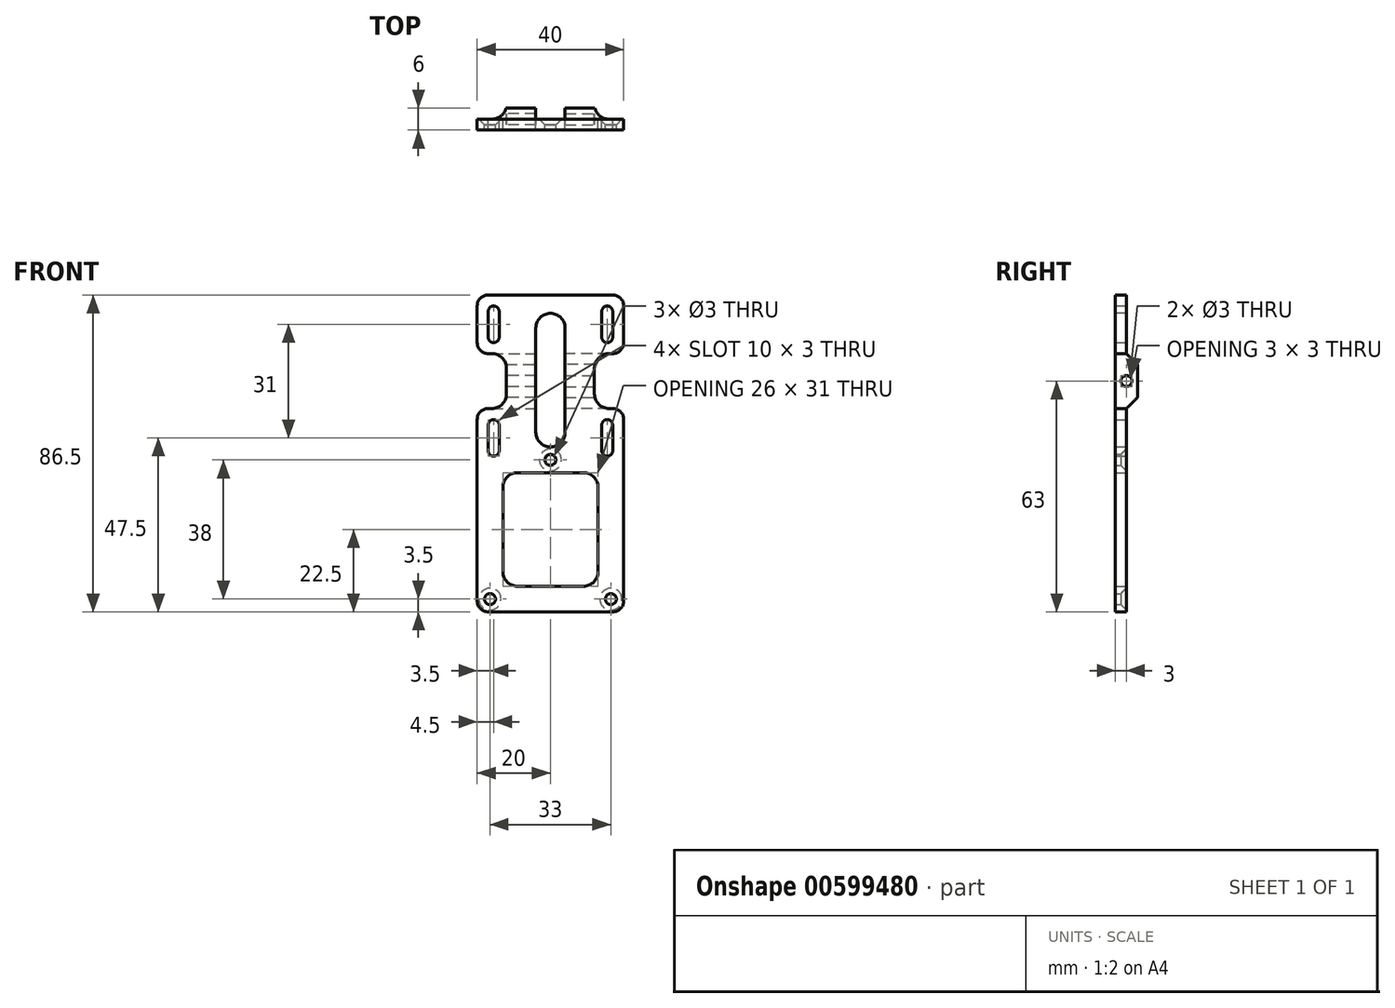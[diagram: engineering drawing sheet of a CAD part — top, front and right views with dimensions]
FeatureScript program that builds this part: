
annotation { "Feature Type Name" : "Feature", "Feature Type Description" : "" }
export const myFeature = defineFeature(function(context is Context, id is Id, definition is map)
    precondition{}
    {
        {
            var Q0;
            Q0=qCreatedBy(makeId("Front.planeOp"),FACE);
            var sketch = newSketch(context, id + "F0", { "sketchPlane" : qUnion([Q0])});
            skLineSegment(sketch, "E0.bottom", {"start": v(0, 43.25) * mm, "end": v(-20, 43.25) * mm});
            skLineSegment(sketch, "E0.top", {"start": v(0, -43.25) * mm, "end": v(-20, -43.25) * mm});
            skLineSegment(sketch, "E0.left", {"start": v(0, 43.25) * mm, "end": v(0, -43.25) * mm});
            skLineSegment(sketch, "E0.right", {"start": v(-20, 43.25) * mm, "end": v(-20, -43.25) * mm});
            skPoint(sketch, "E1", {"position": v(0, 0) * mm});
            skPoint(sketch, "E2", {"position": v(-16.5, -39.75) * mm});
            skPoint(sketch, "E3", {"position": v(0, -1.75) * mm});
            skLineSegment(sketch, "E4.bottom", {"start": v(-14, -0.75) * mm, "end": v(-17, -0.75) * mm});
            skLineSegment(sketch, "E4.top", {"start": v(-14, 9.25) * mm, "end": v(-17, 9.25) * mm});
            skLineSegment(sketch, "E4.left", {"start": v(-14, -0.75) * mm, "end": v(-14, 9.25) * mm});
            skLineSegment(sketch, "E4.right", {"start": v(-17, -0.75) * mm, "end": v(-17, 9.25) * mm});
            skLineSegment(sketch, "E5", {"start": v(0, 19.75) * mm, "end": v(-20, 19.75) * mm, "construction": true});
            skPoint(sketch, "E6", {"position": v(-14, 4.25) * mm});
            skLineSegment(sketch, "E7.MirrorCS", {"start": v(-14, 30.25) * mm, "end": v(-17, 30.25) * mm});
            skLineSegment(sketch, "E8.MirrorCS", {"start": v(-14, 40.25) * mm, "end": v(-14, 30.25) * mm});
            skLineSegment(sketch, "E9.MirrorCS", {"start": v(-17, 40.25) * mm, "end": v(-17, 30.25) * mm});
            skLineSegment(sketch, "E10.MirrorCS", {"start": v(-14, 40.25) * mm, "end": v(-17, 40.25) * mm});
            skLineSegment(sketch, "E11", {"start": v(0, 38.25) * mm, "end": v(-4, 38.25) * mm});
            skLineSegment(sketch, "E12", {"start": v(-4, 38.25) * mm, "end": v(-4, 1.75) * mm});
            skLineSegment(sketch, "E13", {"start": v(-4, 1.75) * mm, "end": v(0, 1.75) * mm});
            skLineSegment(sketch, "E14", {"start": v(0, -36.25) * mm, "end": v(-13, -36.25) * mm});
            skLineSegment(sketch, "E15", {"start": v(-13, -36.25) * mm, "end": v(-13, -5.25) * mm});
            skLineSegment(sketch, "E16", {"start": v(-13, -5.25) * mm, "end": v(0, -5.25) * mm});
            skPoint(sketch, "E17", {"position": v(-15.5, -0.75) * mm});
            skLineSegment(sketch, "E18", {"start": v(-20, 12.25) * mm, "end": v(-12, 12.25) * mm});
            skLineSegment(sketch, "E19", {"start": v(-12, 12.25) * mm, "end": v(-12, 19.75) * mm});
            skLineSegment(sketch, "E20.MirrorCS", {"start": v(-12, 27.25) * mm, "end": v(-12, 19.75) * mm});
            skLineSegment(sketch, "E21.MirrorCS", {"start": v(-20, 27.25) * mm, "end": v(-12, 27.25) * mm});
            skLineSegment(sketch, "E22", {"start": v(-12, 27.25) * mm, "end": v(-4, 27.25) * mm});
            skLineSegment(sketch, "E23", {"start": v(-12, 12.25) * mm, "end": v(-4, 12.25) * mm});
            skSolve(sketch);
        }
        {
            var Q0;
            Q0=makeQuery(id+"F0.imprint","IMPRINT",FACE,{"disambiguationData":[TD([[makeQuery(id+"F0.imprint","IMPRINT",EDGE,{"derivedFrom":sQuery(id+"F0.wireOp",EDGE,"E0.bottom")}),1.0]])]});
            var Q1;
            {var subQ0=sQuery(id+"F0.wireOp",EDGE,"vfTZMCeK-eEZJ-BKLE-hduP-PeNeDjFpHONc");Q1=makeQuery(id+"F0.imprint","IMPRINT",FACE,{"disambiguationData":[TD([[makeQuery(id+"F0.imprint","IMPRINT",EDGE,{"derivedFrom":subQ0}),-1.0]])]});}
            var Q2;
            {var subQ3=sQuery(id+"F0.wireOp",EDGE,"E0.top");Q2=makeQuery(id+"F0.imprint","IMPRINT",FACE,{"disambiguationData":[TD([[makeQuery(id+"F0.imprint","IMPRINT",EDGE,{"derivedFrom":subQ3}),-1.0]])]});}
            var Q3;
            Q3=makeQuery(id+"F0.imprint","IMPRINT",FACE,{"disambiguationData":[TD([[makeQuery(id+"F0.imprint","IMPRINT",EDGE,{"derivedFrom":sQuery(id+"F0.wireOp",EDGE,"E19")}),-1.0]])]});
            extrude(context, id + "F1", {"entities" : qUnion([Q0, Q1, Q2, Q3]), "depth" : 3 * mm, "offsetDistance" : 25 * mm});
        }
        {
            var Q0;
            Q0=sQuery(id+"F0.wireOp",VERTEX,"E3");
            var Q1;
            Q1=sQuery(id+"F0.wireOp",VERTEX,"E2");
            var Q2;
            Q2=makeQuery(id+"F1.opExtrude","SWEPT_BODY",BODY,{"disambiguationData":[OSD([sQuery(id+"F0.wireOp",EDGE,"E0.bottom"),sQuery(id+"F0.wireOp",EDGE,"E0.top"),sQuery(id+"F0.wireOp",EDGE,"E0.left"),sQuery(id+"F0.wireOp",EDGE,"E0.right"),sQuery(id+"F0.wireOp",EDGE,"E4.bottom"),sQuery(id+"F0.wireOp",EDGE,"E4.top"),sQuery(id+"F0.wireOp",EDGE,"E4.left"),sQuery(id+"F0.wireOp",EDGE,"E4.right"),sQuery(id+"F0.wireOp",EDGE,"E7.MirrorCS"),sQuery(id+"F0.wireOp",EDGE,"E8.MirrorCS"),sQuery(id+"F0.wireOp",EDGE,"E9.MirrorCS"),sQuery(id+"F0.wireOp",EDGE,"E10.MirrorCS")])]});
            hole(context, id + "F2", {"style" : HoleStyle.C_SINK, "endStyle" : HoleEndStyle.THROUGH, "oppositeDirection" : true, "holeDiameter" : 3 * mm, "cSinkDiameter" : 6 * mm, "cSinkAngle" : 90 * degree, "majorDiameter" : 5 * mm, "isTappedThrough" : true, "tappedDepth" : 12 * mm, "tapClearance" : 3, "locations" : qUnion([Q0, Q1]), "scope" : qUnion([Q2])});
        }
        {
            var Q0;
            Q0=makeQuery(id+"F1.opExtrude","SWEPT_EDGE",EDGE,{"disambiguationData":[OSD([sQuery(id+"F0.wireOp",EDGE,"E4.bottom"),sQuery(id+"F0.wireOp",EDGE,"E4.left")])]});
            var Q1;
            Q1=makeQuery(id+"F1.opExtrude","SWEPT_EDGE",EDGE,{"disambiguationData":[OSD([sQuery(id+"F0.wireOp",EDGE,"E4.bottom"),sQuery(id+"F0.wireOp",EDGE,"E4.right")])]});
            var Q2;
            Q2=makeQuery(id+"F1.opExtrude","SWEPT_EDGE",EDGE,{"disambiguationData":[OSD([sQuery(id+"F0.wireOp",EDGE,"E4.top"),sQuery(id+"F0.wireOp",EDGE,"E4.right")])]});
            var Q3;
            Q3=makeQuery(id+"F1.opExtrude","SWEPT_EDGE",EDGE,{"disambiguationData":[OSD([sQuery(id+"F0.wireOp",EDGE,"E4.top"),sQuery(id+"F0.wireOp",EDGE,"E4.left")])]});
            var Q4;
            Q4=makeQuery(id+"F1.opExtrude","SWEPT_EDGE",EDGE,{"disambiguationData":[OSD([sQuery(id+"F0.wireOp",EDGE,"E8.MirrorCS"),sQuery(id+"F0.wireOp",EDGE,"E10.MirrorCS")])]});
            var Q5;
            Q5=makeQuery(id+"F1.opExtrude","SWEPT_EDGE",EDGE,{"disambiguationData":[OSD([sQuery(id+"F0.wireOp",EDGE,"E9.MirrorCS"),sQuery(id+"F0.wireOp",EDGE,"E10.MirrorCS")])]});
            var Q6;
            Q6=makeQuery(id+"F1.opExtrude","SWEPT_EDGE",EDGE,{"disambiguationData":[OSD([sQuery(id+"F0.wireOp",EDGE,"E7.MirrorCS"),sQuery(id+"F0.wireOp",EDGE,"E9.MirrorCS")])]});
            var Q7;
            Q7=makeQuery(id+"F1.opExtrude","SWEPT_EDGE",EDGE,{"disambiguationData":[OSD([sQuery(id+"F0.wireOp",EDGE,"E7.MirrorCS"),sQuery(id+"F0.wireOp",EDGE,"E8.MirrorCS")])]});
            fillet(context, id + "F3", {"entities" : qUnion([Q0, Q1, Q2, Q3, Q4, Q5, Q6, Q7]), "radius" : 1.5 * mm, "tangentPropagation" : true, "allowEdgeOverflow" : false});
        }
        {
            var Q0;
            Q0=makeQuery(id+"F1.opExtrude","SWEPT_EDGE",EDGE,{"disambiguationData":[OSD([sQuery(id+"F0.wireOp",EDGE,"E0.bottom"),sQuery(id+"F0.wireOp",EDGE,"E0.right")])]});
            var Q1;
            Q1=makeQuery(id+"F1.opExtrude","SWEPT_EDGE",EDGE,{"disambiguationData":[OSD([sQuery(id+"F0.wireOp",EDGE,"E0.top"),sQuery(id+"F0.wireOp",EDGE,"E0.right")])]});
            var Q2;
            Q2=makeQuery(id+"F1.opExtrude","SWEPT_EDGE",EDGE,{"disambiguationData":[OSD([sQuery(id+"F0.wireOp",EDGE,"E0.right"),sQuery(id+"F0.wireOp",EDGE,"E18")])]});
            var Q3;
            Q3=makeQuery(id+"F1.opExtrude","SWEPT_EDGE",EDGE,{"disambiguationData":[OSD([sQuery(id+"F0.wireOp",EDGE,"E0.right"),sQuery(id+"F0.wireOp",EDGE,"E21.MirrorCS")])]});
            fillet(context, id + "F4", {"entities" : qUnion([Q0, Q1, Q2, Q3]), "radius" : 3 * mm, "tangentPropagation" : true, "allowEdgeOverflow" : false});
        }
        {
            var Q0;
            Q0=makeQuery(id+"F0.imprint","IMPRINT",FACE,{"disambiguationData":[TD([[makeQuery(id+"F0.imprint","IMPRINT",EDGE,{"derivedFrom":sQuery(id+"F0.wireOp",EDGE,"E19")}),-1.0]])]});
            extrude(context, id + "F5", {"entities" : qUnion([Q0]), "operationType" : NewBodyOperationType.ADD, "oppositeDirection" : true, "depth" : 3 * mm, "offsetDistance" : 25 * mm});
        }
        {
            var Q0;
            Q0=makeQuery(id+"F5.opExtrude","CAP_EDGE",EDGE,{"disambiguationData":[OSD([sQuery(id+"F0.wireOp",EDGE,"E23")])],"isStart":false});
            var Q1;
            Q1=makeQuery(id+"F5.opExtrude","CAP_EDGE",EDGE,{"disambiguationData":[OSD([sQuery(id+"F0.wireOp",EDGE,"E22")])],"isStart":false});
            chamfer(context, id + "F6", {"entities" : qUnion([Q0, Q1]), "width" : 3 * mm, "tangentPropagation" : true});
        }
        {
            var Q0;
            Q0=makeQuery(id+"F1.opExtrude","SWEPT_EDGE",EDGE,{"disambiguationData":[OSD([sQuery(id+"F0.wireOp",EDGE,"E12"),sQuery(id+"F0.wireOp",EDGE,"E13")])]});
            var Q1;
            Q1=makeQuery(id+"F1.opExtrude","SWEPT_EDGE",EDGE,{"disambiguationData":[OSD([sQuery(id+"F0.wireOp",EDGE,"E11"),sQuery(id+"F0.wireOp",EDGE,"E12")])]});
            var Q2;
            Q2=makeQuery(id+"F1.opExtrude","SWEPT_EDGE",EDGE,{"disambiguationData":[OSD([sQuery(id+"F0.wireOp",EDGE,"E15"),sQuery(id+"F0.wireOp",EDGE,"E16")])]});
            var Q3;
            Q3=makeQuery(id+"F1.opExtrude","SWEPT_EDGE",EDGE,{"disambiguationData":[OSD([sQuery(id+"F0.wireOp",EDGE,"E14"),sQuery(id+"F0.wireOp",EDGE,"E15")])]});
            var Q4;
            Q4=makeQuery(id+"F1.opExtrude","SWEPT_EDGE",EDGE,{"disambiguationData":[OSD([sQuery(id+"F0.wireOp",EDGE,"E20.MirrorCS"),sQuery(id+"F0.wireOp",EDGE,"E21.MirrorCS"),sQuery(id+"F0.wireOp",EDGE,"E22")])]});
            var Q5;
            Q5=makeQuery(id+"F1.opExtrude","SWEPT_EDGE",EDGE,{"disambiguationData":[OSD([sQuery(id+"F0.wireOp",EDGE,"E18"),sQuery(id+"F0.wireOp",EDGE,"E19"),sQuery(id+"F0.wireOp",EDGE,"E23")])]});
            fillet(context, id + "F7", {"entities" : qUnion([Q0, Q1, Q2, Q3, Q4, Q5]), "radius" : 4 * mm, "tangentPropagation" : true, "allowEdgeOverflow" : false});
        }
        {
            var Q0;
            {var subQ0=sQuery(id+"F0.wireOp",EDGE,"E20.MirrorCS");var subQ1=sQuery(id+"F0.wireOp",EDGE,"E19");Q0=makeQuery(id+"F5.boolean.opBoolean","MERGE",FACE,{"derivedFrom":[makeQuery(id+"F1.opExtrude","SWEPT_FACE",FACE,{"disambiguationData":[OSD([subQ1,subQ0])]}),makeQuery(id+"F5.opExtrude","SWEPT_FACE",FACE,{"disambiguationData":[OSD([subQ1,subQ0])]})]});}
            var sketch = newSketch(context, id + "F8", { "sketchPlane" : qUnion([Q0])});
            skPoint(sketch, "E24", {"position": v(0, 19.75) * mm});
            skPoint(sketch, "E24.positionSnap0", {"position": v(0, 23.25) * mm});
            skPoint(sketch, "E24.positionSnap1", {"position": v(3, 19.75) * mm});
            skSolve(sketch);
        }
        {
            var Q0;
            Q0=sQuery(id+"F8.wireOp",VERTEX,"E24");
            var Q1;
            Q1=makeQuery(id+"F1.opExtrude","SWEPT_BODY",BODY,{"disambiguationData":[OSD([sQuery(id+"F0.wireOp",EDGE,"E0.bottom"),sQuery(id+"F0.wireOp",EDGE,"E0.top"),sQuery(id+"F0.wireOp",EDGE,"E0.left"),sQuery(id+"F0.wireOp",EDGE,"E0.right"),sQuery(id+"F0.wireOp",EDGE,"E4.bottom"),sQuery(id+"F0.wireOp",EDGE,"E4.top"),sQuery(id+"F0.wireOp",EDGE,"E4.left"),sQuery(id+"F0.wireOp",EDGE,"E4.right"),sQuery(id+"F0.wireOp",EDGE,"E7.MirrorCS"),sQuery(id+"F0.wireOp",EDGE,"E8.MirrorCS"),sQuery(id+"F0.wireOp",EDGE,"E9.MirrorCS"),sQuery(id+"F0.wireOp",EDGE,"E10.MirrorCS"),sQuery(id+"F0.wireOp",EDGE,"E11"),sQuery(id+"F0.wireOp",EDGE,"E12"),sQuery(id+"F0.wireOp",EDGE,"E13"),sQuery(id+"F0.wireOp",EDGE,"E14"),sQuery(id+"F0.wireOp",EDGE,"E15"),sQuery(id+"F0.wireOp",EDGE,"E16"),sQuery(id+"F0.wireOp",EDGE,"E18"),sQuery(id+"F0.wireOp",EDGE,"E19"),sQuery(id+"F0.wireOp",EDGE,"E20.MirrorCS"),sQuery(id+"F0.wireOp",EDGE,"E21.MirrorCS")])]});
            hole(context, id + "F9", {"style" : HoleStyle.SIMPLE, "endStyle" : HoleEndStyle.THROUGH, "holeDiameter" : 3 * mm, "majorDiameter" : 5 * mm, "isTappedThrough" : true, "tappedDepth" : 12 * mm, "tapClearance" : 3, "locations" : qUnion([Q0]), "scope" : qUnion([Q1])});
        }
        {
            var Q0;
            Q0=makeQuery(id+"F1.opExtrude","SWEPT_BODY",BODY,{"disambiguationData":[OSD([sQuery(id+"F0.wireOp",EDGE,"E0.bottom"),sQuery(id+"F0.wireOp",EDGE,"E0.top"),sQuery(id+"F0.wireOp",EDGE,"E0.left"),sQuery(id+"F0.wireOp",EDGE,"E0.right"),sQuery(id+"F0.wireOp",EDGE,"E4.bottom"),sQuery(id+"F0.wireOp",EDGE,"E4.top"),sQuery(id+"F0.wireOp",EDGE,"E4.left"),sQuery(id+"F0.wireOp",EDGE,"E4.right"),sQuery(id+"F0.wireOp",EDGE,"E7.MirrorCS"),sQuery(id+"F0.wireOp",EDGE,"E8.MirrorCS"),sQuery(id+"F0.wireOp",EDGE,"E9.MirrorCS"),sQuery(id+"F0.wireOp",EDGE,"E10.MirrorCS"),sQuery(id+"F0.wireOp",EDGE,"E11"),sQuery(id+"F0.wireOp",EDGE,"E12"),sQuery(id+"F0.wireOp",EDGE,"E13")])]});
            var Q1;
            Q1=qCreatedBy(makeId("Right.planeOp"),FACE);
            mirror(context, id + "F10", {"operationType" : NewBodyOperationType.ADD, "entities" : qUnion([Q0]), "mirrorPlane" : qUnion([Q1])});
        }
    });
